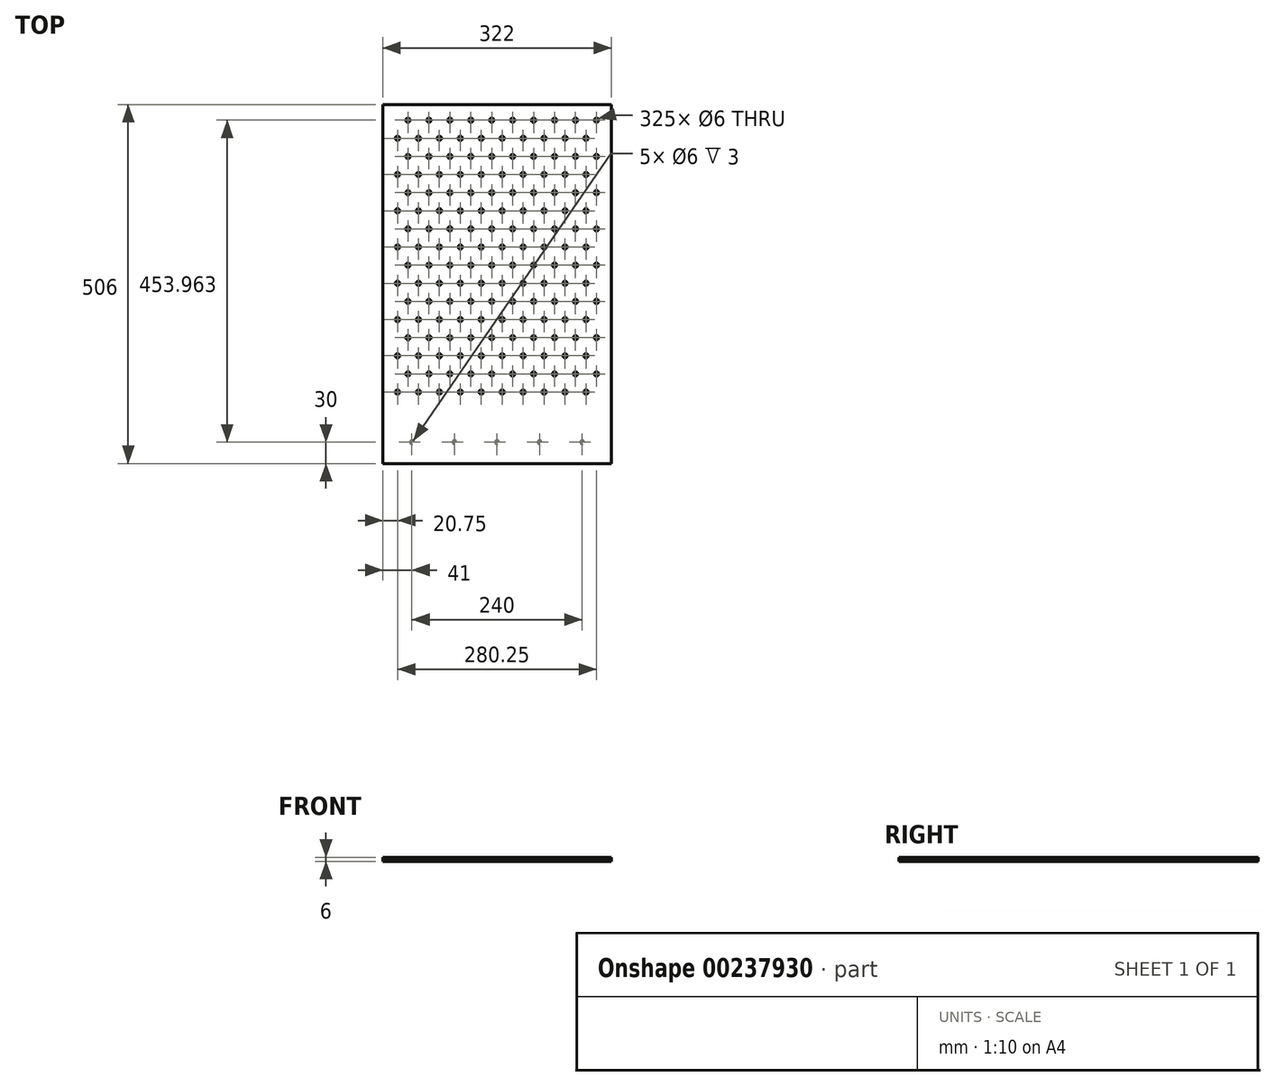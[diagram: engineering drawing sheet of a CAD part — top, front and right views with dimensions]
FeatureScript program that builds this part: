
annotation { "Feature Type Name" : "Feature", "Feature Type Description" : "" }
export const myFeature = defineFeature(function(context is Context, id is Id, definition is map)
    precondition{}
    {
        {
            var Q0;
            Q0=qCreatedBy(makeId("Top.planeOp"),FACE);
            var sketch = newSketch(context, id + "F0", { "sketchPlane" : qUnion([Q0])});
            skCircle(sketch, "E0", {"center": v(0, 0) * mm, "radius": 14.75 * mm, "construction": true});
            skLineSegment(sketch, "E1", {"start": v(-14.75, 59.88) * mm, "end": v(-14.75, -39.27) * mm, "construction": true});
            skLineSegment(sketch, "E2", {"start": v(-42.71, -14.75) * mm, "end": v(49.2, -14.75) * mm, "construction": true});
            skLineSegment(sketch, "E3.direction1", {"start": v(0, 0) * mm, "end": v(29.5, 0) * mm, "construction": true});
            skLineSegment(sketch, "E3.direction2", {"start": v(0, -297.48) * mm, "end": v(0, 0) * mm, "construction": true});
            skCircle(sketch, "E4", {"center": v(0, 0) * mm, "radius": 3 * mm});
            skCircle(sketch, "E5.0.1.0", {"center": v(0, 51.1) * mm, "radius": 3 * mm});
            skCircle(sketch, "E5.0.2.0", {"center": v(0, 102.19) * mm, "radius": 3 * mm});
            skCircle(sketch, "E5.0.3.0", {"center": v(0, 153.28) * mm, "radius": 3 * mm});
            skCircle(sketch, "E5.0.4.0", {"center": v(0, 204.38) * mm, "radius": 3 * mm});
            skCircle(sketch, "E5.0.5.0", {"center": v(0, 255.47) * mm, "radius": 3 * mm});
            skCircle(sketch, "E5.1.0.0", {"center": v(29.5, 0) * mm, "radius": 3 * mm});
            skCircle(sketch, "E5.1.1.0", {"center": v(29.5, 51.1) * mm, "radius": 3 * mm});
            skCircle(sketch, "E5.1.2.0", {"center": v(29.5, 102.19) * mm, "radius": 3 * mm});
            skCircle(sketch, "E5.1.3.0", {"center": v(29.5, 153.28) * mm, "radius": 3 * mm});
            skCircle(sketch, "E5.1.4.0", {"center": v(29.5, 204.38) * mm, "radius": 3 * mm});
            skCircle(sketch, "E5.1.5.0", {"center": v(29.5, 255.47) * mm, "radius": 3 * mm});
            skCircle(sketch, "E5.2.0.0", {"center": v(59, 0) * mm, "radius": 3 * mm});
            skCircle(sketch, "E5.2.1.0", {"center": v(59, 51.1) * mm, "radius": 3 * mm});
            skCircle(sketch, "E5.2.2.0", {"center": v(59, 102.19) * mm, "radius": 3 * mm});
            skCircle(sketch, "E5.2.3.0", {"center": v(59, 153.28) * mm, "radius": 3 * mm});
            skCircle(sketch, "E5.2.4.0", {"center": v(59, 204.38) * mm, "radius": 3 * mm});
            skCircle(sketch, "E5.2.5.0", {"center": v(59, 255.47) * mm, "radius": 3 * mm});
            skCircle(sketch, "E5.3.0.0", {"center": v(88.5, 0) * mm, "radius": 3 * mm});
            skCircle(sketch, "E5.3.1.0", {"center": v(88.5, 51.1) * mm, "radius": 3 * mm});
            skCircle(sketch, "E5.3.2.0", {"center": v(88.5, 102.19) * mm, "radius": 3 * mm});
            skCircle(sketch, "E5.3.3.0", {"center": v(88.5, 153.28) * mm, "radius": 3 * mm});
            skCircle(sketch, "E5.3.4.0", {"center": v(88.5, 204.38) * mm, "radius": 3 * mm});
            skCircle(sketch, "E5.3.5.0", {"center": v(88.5, 255.47) * mm, "radius": 3 * mm});
            skCircle(sketch, "E5.4.0.0", {"center": v(118, 0) * mm, "radius": 3 * mm});
            skCircle(sketch, "E5.4.1.0", {"center": v(118, 51.1) * mm, "radius": 3 * mm});
            skCircle(sketch, "E5.4.2.0", {"center": v(118, 102.19) * mm, "radius": 3 * mm});
            skCircle(sketch, "E5.4.3.0", {"center": v(118, 153.28) * mm, "radius": 3 * mm});
            skCircle(sketch, "E5.4.4.0", {"center": v(118, 204.38) * mm, "radius": 3 * mm});
            skCircle(sketch, "E5.4.5.0", {"center": v(118, 255.47) * mm, "radius": 3 * mm});
            skCircle(sketch, "E5.5.0.0", {"center": v(147.5, 0) * mm, "radius": 3 * mm});
            skCircle(sketch, "E5.5.1.0", {"center": v(147.5, 51.1) * mm, "radius": 3 * mm});
            skCircle(sketch, "E5.5.2.0", {"center": v(147.5, 102.19) * mm, "radius": 3 * mm});
            skCircle(sketch, "E5.5.3.0", {"center": v(147.5, 153.28) * mm, "radius": 3 * mm});
            skCircle(sketch, "E5.5.4.0", {"center": v(147.5, 204.38) * mm, "radius": 3 * mm});
            skCircle(sketch, "E5.5.5.0", {"center": v(147.5, 255.47) * mm, "radius": 3 * mm});
            skCircle(sketch, "E5.6.0.0", {"center": v(177, 0) * mm, "radius": 3 * mm});
            skCircle(sketch, "E5.6.1.0", {"center": v(177, 51.1) * mm, "radius": 3 * mm});
            skCircle(sketch, "E5.6.2.0", {"center": v(177, 102.19) * mm, "radius": 3 * mm});
            skCircle(sketch, "E5.6.3.0", {"center": v(177, 153.28) * mm, "radius": 3 * mm});
            skCircle(sketch, "E5.6.4.0", {"center": v(177, 204.38) * mm, "radius": 3 * mm});
            skCircle(sketch, "E5.6.5.0", {"center": v(177, 255.47) * mm, "radius": 3 * mm});
            skLineSegment(sketch, "E5.direction2", {"start": v(0, 0) * mm, "end": v(0, 51.1) * mm, "construction": true});
            skLineSegment(sketch, "E6", {"start": v(-14.75, -14.75) * mm, "end": v(295.25, -14.75) * mm, "construction": true});
            skPoint(sketch, "E6.endSnap0", {"position": v(3.24, -14.75) * mm});
            skLineSegment(sketch, "E7", {"start": v(295.25, -14.75) * mm, "end": v(295.25, 395.25) * mm, "construction": true});
            skLineSegment(sketch, "E8", {"start": v(295.25, 395.25) * mm, "end": v(-14.75, 395.25) * mm, "construction": true});
            skLineSegment(sketch, "E9", {"start": v(-14.75, 395.25) * mm, "end": v(-14.75, -14.75) * mm, "construction": true});
            skCircle(sketch, "E10.0.7.0", {"center": v(206.5, 0) * mm, "radius": 3 * mm});
            skCircle(sketch, "E10.0.7.1", {"center": v(206.5, 51.1) * mm, "radius": 3 * mm});
            skCircle(sketch, "E10.0.7.2", {"center": v(206.5, 102.19) * mm, "radius": 3 * mm});
            skCircle(sketch, "E10.0.7.3", {"center": v(206.5, 153.28) * mm, "radius": 3 * mm});
            skCircle(sketch, "E10.0.7.4", {"center": v(206.5, 204.38) * mm, "radius": 3 * mm});
            skCircle(sketch, "E10.0.7.5", {"center": v(206.5, 255.47) * mm, "radius": 3 * mm});
            skCircle(sketch, "E10.0.8.0", {"center": v(236, 0) * mm, "radius": 3 * mm});
            skCircle(sketch, "E10.0.8.1", {"center": v(236, 51.1) * mm, "radius": 3 * mm});
            skCircle(sketch, "E10.0.8.2", {"center": v(236, 102.19) * mm, "radius": 3 * mm});
            skCircle(sketch, "E10.0.8.3", {"center": v(236, 153.28) * mm, "radius": 3 * mm});
            skCircle(sketch, "E10.0.8.4", {"center": v(236, 204.38) * mm, "radius": 3 * mm});
            skCircle(sketch, "E10.0.8.5", {"center": v(236, 255.47) * mm, "radius": 3 * mm});
            skCircle(sketch, "E11.0.9.0", {"center": v(265.5, 0) * mm, "radius": 3 * mm});
            skCircle(sketch, "E11.0.9.1", {"center": v(265.5, 51.1) * mm, "radius": 3 * mm});
            skCircle(sketch, "E11.0.9.2", {"center": v(265.5, 102.19) * mm, "radius": 3 * mm});
            skCircle(sketch, "E11.0.9.3", {"center": v(265.5, 153.28) * mm, "radius": 3 * mm});
            skCircle(sketch, "E11.0.9.4", {"center": v(265.5, 204.38) * mm, "radius": 3 * mm});
            skCircle(sketch, "E11.0.9.5", {"center": v(265.5, 255.47) * mm, "radius": 3 * mm});
            skLineSegment(sketch, "E12", {"start": v(-20.75, 405.25) * mm, "end": v(301.25, 405.25) * mm});
            skLineSegment(sketch, "E13", {"start": v(301.25, 405.25) * mm, "end": v(301.25, -100.75) * mm});
            skLineSegment(sketch, "E14", {"start": v(301.25, -100.75) * mm, "end": v(-20.75, -100.75) * mm});
            skLineSegment(sketch, "E15", {"start": v(-20.75, -100.75) * mm, "end": v(-20.75, 405.25) * mm});
            skCircle(sketch, "E16", {"center": v(29.5, 0) * mm, "radius": 14.75 * mm, "construction": true});
            skCircle(sketch, "E17", {"center": v(14.75, 25.55) * mm, "radius": 14.75 * mm, "construction": true});
            skCircle(sketch, "E18", {"center": v(0, 51.1) * mm, "radius": 14.75 * mm, "construction": true});
            skCircle(sketch, "E19.0.0.6", {"center": v(0, 306.57) * mm, "radius": 3 * mm});
            skCircle(sketch, "E19.0.0.7", {"center": v(0, 357.67) * mm, "radius": 3 * mm});
            skCircle(sketch, "E19.0.1.6", {"center": v(29.5, 306.57) * mm, "radius": 3 * mm});
            skCircle(sketch, "E19.0.1.7", {"center": v(29.5, 357.67) * mm, "radius": 3 * mm});
            skCircle(sketch, "E19.0.2.6", {"center": v(59, 306.57) * mm, "radius": 3 * mm});
            skCircle(sketch, "E19.0.2.7", {"center": v(59, 357.67) * mm, "radius": 3 * mm});
            skCircle(sketch, "E19.0.3.6", {"center": v(88.5, 306.57) * mm, "radius": 3 * mm});
            skCircle(sketch, "E19.0.3.7", {"center": v(88.5, 357.67) * mm, "radius": 3 * mm});
            skCircle(sketch, "E19.0.4.6", {"center": v(118, 306.57) * mm, "radius": 3 * mm});
            skCircle(sketch, "E19.0.4.7", {"center": v(118, 357.67) * mm, "radius": 3 * mm});
            skCircle(sketch, "E19.0.5.6", {"center": v(147.5, 306.57) * mm, "radius": 3 * mm});
            skCircle(sketch, "E19.0.5.7", {"center": v(147.5, 357.67) * mm, "radius": 3 * mm});
            skCircle(sketch, "E19.0.6.6", {"center": v(177, 306.57) * mm, "radius": 3 * mm});
            skCircle(sketch, "E19.0.6.7", {"center": v(177, 357.67) * mm, "radius": 3 * mm});
            skCircle(sketch, "E19.0.7.6", {"center": v(206.5, 306.57) * mm, "radius": 3 * mm});
            skCircle(sketch, "E19.0.7.7", {"center": v(206.5, 357.67) * mm, "radius": 3 * mm});
            skCircle(sketch, "E19.0.8.6", {"center": v(236, 306.57) * mm, "radius": 3 * mm});
            skCircle(sketch, "E19.0.8.7", {"center": v(236, 357.67) * mm, "radius": 3 * mm});
            skCircle(sketch, "E19.0.9.6", {"center": v(265.5, 306.57) * mm, "radius": 3 * mm});
            skCircle(sketch, "E19.0.9.7", {"center": v(265.5, 357.67) * mm, "radius": 3 * mm});
            skCircle(sketch, "E20", {"center": v(14.75, 25.55) * mm, "radius": 3 * mm});
            skCircle(sketch, "E21.0.1.0", {"center": v(14.75, 76.64) * mm, "radius": 3 * mm});
            skCircle(sketch, "E21.0.2.0", {"center": v(14.75, 127.74) * mm, "radius": 3 * mm});
            skCircle(sketch, "E21.0.3.0", {"center": v(14.75, 178.83) * mm, "radius": 3 * mm});
            skCircle(sketch, "E21.0.4.0", {"center": v(14.75, 229.93) * mm, "radius": 3 * mm});
            skCircle(sketch, "E21.0.5.0", {"center": v(14.75, 281.02) * mm, "radius": 3 * mm});
            skCircle(sketch, "E21.0.6.0", {"center": v(14.75, 332.12) * mm, "radius": 3 * mm});
            skCircle(sketch, "E21.1.0.0", {"center": v(44.25, 25.55) * mm, "radius": 3 * mm});
            skCircle(sketch, "E21.1.1.0", {"center": v(44.25, 76.64) * mm, "radius": 3 * mm});
            skCircle(sketch, "E21.1.2.0", {"center": v(44.25, 127.74) * mm, "radius": 3 * mm});
            skCircle(sketch, "E21.1.3.0", {"center": v(44.25, 178.83) * mm, "radius": 3 * mm});
            skCircle(sketch, "E21.1.4.0", {"center": v(44.25, 229.93) * mm, "radius": 3 * mm});
            skCircle(sketch, "E21.1.5.0", {"center": v(44.25, 281.02) * mm, "radius": 3 * mm});
            skCircle(sketch, "E21.1.6.0", {"center": v(44.25, 332.12) * mm, "radius": 3 * mm});
            skCircle(sketch, "E21.2.0.0", {"center": v(73.75, 25.55) * mm, "radius": 3 * mm});
            skCircle(sketch, "E21.2.1.0", {"center": v(73.75, 76.64) * mm, "radius": 3 * mm});
            skCircle(sketch, "E21.2.2.0", {"center": v(73.75, 127.74) * mm, "radius": 3 * mm});
            skCircle(sketch, "E21.2.3.0", {"center": v(73.75, 178.83) * mm, "radius": 3 * mm});
            skCircle(sketch, "E21.2.4.0", {"center": v(73.75, 229.93) * mm, "radius": 3 * mm});
            skCircle(sketch, "E21.2.5.0", {"center": v(73.75, 281.02) * mm, "radius": 3 * mm});
            skCircle(sketch, "E21.2.6.0", {"center": v(73.75, 332.12) * mm, "radius": 3 * mm});
            skCircle(sketch, "E21.3.0.0", {"center": v(103.25, 25.55) * mm, "radius": 3 * mm});
            skCircle(sketch, "E21.3.1.0", {"center": v(103.25, 76.64) * mm, "radius": 3 * mm});
            skCircle(sketch, "E21.3.2.0", {"center": v(103.25, 127.74) * mm, "radius": 3 * mm});
            skCircle(sketch, "E21.3.3.0", {"center": v(103.25, 178.83) * mm, "radius": 3 * mm});
            skCircle(sketch, "E21.3.4.0", {"center": v(103.25, 229.93) * mm, "radius": 3 * mm});
            skCircle(sketch, "E21.3.5.0", {"center": v(103.25, 281.02) * mm, "radius": 3 * mm});
            skCircle(sketch, "E21.3.6.0", {"center": v(103.25, 332.12) * mm, "radius": 3 * mm});
            skCircle(sketch, "E21.4.0.0", {"center": v(132.75, 25.55) * mm, "radius": 3 * mm});
            skCircle(sketch, "E21.4.1.0", {"center": v(132.75, 76.64) * mm, "radius": 3 * mm});
            skCircle(sketch, "E21.4.2.0", {"center": v(132.75, 127.74) * mm, "radius": 3 * mm});
            skCircle(sketch, "E21.4.3.0", {"center": v(132.75, 178.83) * mm, "radius": 3 * mm});
            skCircle(sketch, "E21.4.4.0", {"center": v(132.75, 229.93) * mm, "radius": 3 * mm});
            skCircle(sketch, "E21.4.5.0", {"center": v(132.75, 281.02) * mm, "radius": 3 * mm});
            skCircle(sketch, "E21.4.6.0", {"center": v(132.75, 332.12) * mm, "radius": 3 * mm});
            skCircle(sketch, "E21.5.0.0", {"center": v(162.25, 25.55) * mm, "radius": 3 * mm});
            skCircle(sketch, "E21.5.1.0", {"center": v(162.25, 76.64) * mm, "radius": 3 * mm});
            skCircle(sketch, "E21.5.2.0", {"center": v(162.25, 127.74) * mm, "radius": 3 * mm});
            skCircle(sketch, "E21.5.3.0", {"center": v(162.25, 178.83) * mm, "radius": 3 * mm});
            skCircle(sketch, "E21.5.4.0", {"center": v(162.25, 229.93) * mm, "radius": 3 * mm});
            skCircle(sketch, "E21.5.5.0", {"center": v(162.25, 281.02) * mm, "radius": 3 * mm});
            skCircle(sketch, "E21.5.6.0", {"center": v(162.25, 332.12) * mm, "radius": 3 * mm});
            skCircle(sketch, "E21.6.0.0", {"center": v(191.75, 25.55) * mm, "radius": 3 * mm});
            skCircle(sketch, "E21.6.1.0", {"center": v(191.75, 76.64) * mm, "radius": 3 * mm});
            skCircle(sketch, "E21.6.2.0", {"center": v(191.75, 127.74) * mm, "radius": 3 * mm});
            skCircle(sketch, "E21.6.3.0", {"center": v(191.75, 178.83) * mm, "radius": 3 * mm});
            skCircle(sketch, "E21.6.4.0", {"center": v(191.75, 229.93) * mm, "radius": 3 * mm});
            skCircle(sketch, "E21.6.5.0", {"center": v(191.75, 281.02) * mm, "radius": 3 * mm});
            skCircle(sketch, "E21.6.6.0", {"center": v(191.75, 332.12) * mm, "radius": 3 * mm});
            skCircle(sketch, "E21.7.0.0", {"center": v(221.25, 25.55) * mm, "radius": 3 * mm});
            skCircle(sketch, "E21.7.1.0", {"center": v(221.25, 76.64) * mm, "radius": 3 * mm});
            skCircle(sketch, "E21.7.2.0", {"center": v(221.25, 127.74) * mm, "radius": 3 * mm});
            skCircle(sketch, "E21.7.3.0", {"center": v(221.25, 178.83) * mm, "radius": 3 * mm});
            skCircle(sketch, "E21.7.4.0", {"center": v(221.25, 229.93) * mm, "radius": 3 * mm});
            skCircle(sketch, "E21.7.5.0", {"center": v(221.25, 281.02) * mm, "radius": 3 * mm});
            skCircle(sketch, "E21.7.6.0", {"center": v(221.25, 332.12) * mm, "radius": 3 * mm});
            skCircle(sketch, "E21.8.0.0", {"center": v(250.75, 25.55) * mm, "radius": 3 * mm});
            skCircle(sketch, "E21.8.1.0", {"center": v(250.75, 76.64) * mm, "radius": 3 * mm});
            skCircle(sketch, "E21.8.2.0", {"center": v(250.75, 127.74) * mm, "radius": 3 * mm});
            skCircle(sketch, "E21.8.3.0", {"center": v(250.75, 178.83) * mm, "radius": 3 * mm});
            skCircle(sketch, "E21.8.4.0", {"center": v(250.75, 229.93) * mm, "radius": 3 * mm});
            skCircle(sketch, "E21.8.5.0", {"center": v(250.75, 281.02) * mm, "radius": 3 * mm});
            skCircle(sketch, "E21.8.6.0", {"center": v(250.75, 332.12) * mm, "radius": 3 * mm});
            skCircle(sketch, "E21.9.0.0", {"center": v(280.25, 25.55) * mm, "radius": 3 * mm});
            skCircle(sketch, "E21.9.1.0", {"center": v(280.25, 76.64) * mm, "radius": 3 * mm});
            skCircle(sketch, "E21.9.2.0", {"center": v(280.25, 127.74) * mm, "radius": 3 * mm});
            skCircle(sketch, "E21.9.3.0", {"center": v(280.25, 178.83) * mm, "radius": 3 * mm});
            skCircle(sketch, "E21.9.4.0", {"center": v(280.25, 229.93) * mm, "radius": 3 * mm});
            skCircle(sketch, "E21.9.5.0", {"center": v(280.25, 281.02) * mm, "radius": 3 * mm});
            skCircle(sketch, "E21.9.6.0", {"center": v(280.25, 332.12) * mm, "radius": 3 * mm});
            skLineSegment(sketch, "E21.direction1", {"start": v(14.75, 25.55) * mm, "end": v(44.25, 25.55) * mm, "construction": true});
            skLineSegment(sketch, "E21.direction2", {"start": v(14.75, 25.55) * mm, "end": v(14.75, 76.64) * mm, "construction": true});
            skCircle(sketch, "E22", {"center": v(59, 119.22) * mm, "radius": 14.03 * mm, "construction": true});
            skLineSegment(sketch, "E23.bottom", {"start": v(54, 129.22) * mm, "end": v(64, 129.22) * mm, "construction": true});
            skLineSegment(sketch, "E23.top", {"start": v(54, 109.22) * mm, "end": v(64, 109.22) * mm, "construction": true});
            skLineSegment(sketch, "E23.left", {"start": v(54, 129.22) * mm, "end": v(54, 109.22) * mm, "construction": true});
            skLineSegment(sketch, "E23.right", {"start": v(64, 129.22) * mm, "end": v(64, 109.22) * mm, "construction": true});
            skPoint(sketch, "E24.positionSnap0", {"position": v(54, 119.22) * mm});
            skPoint(sketch, "E24.positionSnap1", {"position": v(59, 129.22) * mm});
            skCircle(sketch, "E25.0.0.7", {"center": v(14.75, 383.21) * mm, "radius": 3 * mm});
            skCircle(sketch, "E25.0.1.7", {"center": v(44.25, 383.21) * mm, "radius": 3 * mm});
            skCircle(sketch, "E25.0.2.7", {"center": v(73.75, 383.21) * mm, "radius": 3 * mm});
            skCircle(sketch, "E25.0.3.7", {"center": v(103.25, 383.21) * mm, "radius": 3 * mm});
            skCircle(sketch, "E25.0.4.7", {"center": v(132.75, 383.21) * mm, "radius": 3 * mm});
            skCircle(sketch, "E25.0.5.7", {"center": v(162.25, 383.21) * mm, "radius": 3 * mm});
            skCircle(sketch, "E25.0.6.7", {"center": v(191.75, 383.21) * mm, "radius": 3 * mm});
            skCircle(sketch, "E25.0.7.7", {"center": v(221.25, 383.21) * mm, "radius": 3 * mm});
            skCircle(sketch, "E25.0.8.7", {"center": v(250.75, 383.21) * mm, "radius": 3 * mm});
            skCircle(sketch, "E25.0.9.7", {"center": v(280.25, 383.21) * mm, "radius": 3 * mm});
            skCircle(sketch, "E26", {"center": v(14.75, 383.21) * mm, "radius": 14.75 * mm, "construction": true});
            skCircle(sketch, "E27", {"center": v(280.25, 25.55) * mm, "radius": 14.75 * mm, "construction": true});
            skSolve(sketch);
        }
        {
            var Q0;
            Q0=makeQuery(id+"F0.imprint","IMPRINT",FACE,{"disambiguationData":[TD([[makeQuery(id+"F0.imprint","IMPRINT",EDGE,{"derivedFrom":sQuery(id+"F0.wireOp",EDGE,"E4")}),-1.0]])]});
            extrude(context, id + "F1", {"entities" : qUnion([Q0]), "depth" : 5 * mm});
        }
        {
            var Q0;
            Q0=makeQuery(id+"F1.opExtrude","CAP_FACE",FACE,{"disambiguationData":[OSD([sQuery(id+"F0.wireOp",EDGE,"E4"),sQuery(id+"F0.wireOp",EDGE,"E5.0.1.0"),sQuery(id+"F0.wireOp",EDGE,"E5.0.2.0"),sQuery(id+"F0.wireOp",EDGE,"E5.0.3.0"),sQuery(id+"F0.wireOp",EDGE,"E5.0.4.0"),sQuery(id+"F0.wireOp",EDGE,"E5.0.5.0"),sQuery(id+"F0.wireOp",EDGE,"E5.1.0.0"),sQuery(id+"F0.wireOp",EDGE,"E5.1.1.0"),sQuery(id+"F0.wireOp",EDGE,"E5.1.2.0"),sQuery(id+"F0.wireOp",EDGE,"E5.1.3.0"),sQuery(id+"F0.wireOp",EDGE,"E5.1.4.0"),sQuery(id+"F0.wireOp",EDGE,"E5.1.5.0"),sQuery(id+"F0.wireOp",EDGE,"E5.2.0.0"),sQuery(id+"F0.wireOp",EDGE,"E5.2.1.0"),sQuery(id+"F0.wireOp",EDGE,"E5.2.2.0"),sQuery(id+"F0.wireOp",EDGE,"E5.2.3.0"),sQuery(id+"F0.wireOp",EDGE,"E5.2.4.0"),sQuery(id+"F0.wireOp",EDGE,"E5.2.5.0"),sQuery(id+"F0.wireOp",EDGE,"E5.3.0.0"),sQuery(id+"F0.wireOp",EDGE,"E5.3.1.0"),sQuery(id+"F0.wireOp",EDGE,"E5.3.2.0"),sQuery(id+"F0.wireOp",EDGE,"E5.3.3.0"),sQuery(id+"F0.wireOp",EDGE,"E5.3.4.0"),sQuery(id+"F0.wireOp",EDGE,"E5.3.5.0"),sQuery(id+"F0.wireOp",EDGE,"E5.4.0.0"),sQuery(id+"F0.wireOp",EDGE,"E5.4.1.0"),sQuery(id+"F0.wireOp",EDGE,"E5.4.2.0"),sQuery(id+"F0.wireOp",EDGE,"E5.4.3.0"),sQuery(id+"F0.wireOp",EDGE,"E5.4.4.0"),sQuery(id+"F0.wireOp",EDGE,"E5.4.5.0"),sQuery(id+"F0.wireOp",EDGE,"E5.5.0.0"),sQuery(id+"F0.wireOp",EDGE,"E5.5.1.0"),sQuery(id+"F0.wireOp",EDGE,"E5.5.2.0"),sQuery(id+"F0.wireOp",EDGE,"E5.5.3.0"),sQuery(id+"F0.wireOp",EDGE,"E5.5.4.0"),sQuery(id+"F0.wireOp",EDGE,"E5.5.5.0"),sQuery(id+"F0.wireOp",EDGE,"E5.6.0.0"),sQuery(id+"F0.wireOp",EDGE,"E5.6.1.0"),sQuery(id+"F0.wireOp",EDGE,"E5.6.2.0"),sQuery(id+"F0.wireOp",EDGE,"E5.6.3.0"),sQuery(id+"F0.wireOp",EDGE,"E5.6.4.0"),sQuery(id+"F0.wireOp",EDGE,"E5.6.5.0"),sQuery(id+"F0.wireOp",EDGE,"E10.0.7.0"),sQuery(id+"F0.wireOp",EDGE,"E10.0.7.1"),sQuery(id+"F0.wireOp",EDGE,"E10.0.7.2"),sQuery(id+"F0.wireOp",EDGE,"E10.0.7.3"),sQuery(id+"F0.wireOp",EDGE,"E10.0.7.4"),sQuery(id+"F0.wireOp",EDGE,"E10.0.7.5"),sQuery(id+"F0.wireOp",EDGE,"E10.0.8.0"),sQuery(id+"F0.wireOp",EDGE,"E10.0.8.1"),sQuery(id+"F0.wireOp",EDGE,"E10.0.8.2"),sQuery(id+"F0.wireOp",EDGE,"E10.0.8.3"),sQuery(id+"F0.wireOp",EDGE,"E10.0.8.4"),sQuery(id+"F0.wireOp",EDGE,"E10.0.8.5"),sQuery(id+"F0.wireOp",EDGE,"E11.0.9.0"),sQuery(id+"F0.wireOp",EDGE,"E11.0.9.1"),sQuery(id+"F0.wireOp",EDGE,"E11.0.9.2"),sQuery(id+"F0.wireOp",EDGE,"E11.0.9.3"),sQuery(id+"F0.wireOp",EDGE,"E11.0.9.4"),sQuery(id+"F0.wireOp",EDGE,"E11.0.9.5"),sQuery(id+"F0.wireOp",EDGE,"E12"),sQuery(id+"F0.wireOp",EDGE,"E13"),sQuery(id+"F0.wireOp",EDGE,"E14"),sQuery(id+"F0.wireOp",EDGE,"E15"),sQuery(id+"F0.wireOp",EDGE,"E19.0.0.6"),sQuery(id+"F0.wireOp",EDGE,"E19.0.0.7"),sQuery(id+"F0.wireOp",EDGE,"E19.0.1.6"),sQuery(id+"F0.wireOp",EDGE,"E19.0.1.7"),sQuery(id+"F0.wireOp",EDGE,"E19.0.2.6"),sQuery(id+"F0.wireOp",EDGE,"E19.0.2.7"),sQuery(id+"F0.wireOp",EDGE,"E19.0.3.6"),sQuery(id+"F0.wireOp",EDGE,"E19.0.3.7"),sQuery(id+"F0.wireOp",EDGE,"E19.0.4.6"),sQuery(id+"F0.wireOp",EDGE,"E19.0.4.7"),sQuery(id+"F0.wireOp",EDGE,"E19.0.5.6"),sQuery(id+"F0.wireOp",EDGE,"E19.0.5.7"),sQuery(id+"F0.wireOp",EDGE,"E19.0.6.6"),sQuery(id+"F0.wireOp",EDGE,"E19.0.6.7"),sQuery(id+"F0.wireOp",EDGE,"E19.0.7.6"),sQuery(id+"F0.wireOp",EDGE,"E19.0.7.7"),sQuery(id+"F0.wireOp",EDGE,"E19.0.8.6"),sQuery(id+"F0.wireOp",EDGE,"E19.0.8.7"),sQuery(id+"F0.wireOp",EDGE,"E19.0.9.6"),sQuery(id+"F0.wireOp",EDGE,"E19.0.9.7"),sQuery(id+"F0.wireOp",EDGE,"E20"),sQuery(id+"F0.wireOp",EDGE,"E21.0.1.0"),sQuery(id+"F0.wireOp",EDGE,"E21.0.2.0"),sQuery(id+"F0.wireOp",EDGE,"E21.0.3.0"),sQuery(id+"F0.wireOp",EDGE,"E21.0.4.0"),sQuery(id+"F0.wireOp",EDGE,"E21.0.5.0"),sQuery(id+"F0.wireOp",EDGE,"E21.0.6.0"),sQuery(id+"F0.wireOp",EDGE,"E21.1.0.0"),sQuery(id+"F0.wireOp",EDGE,"E21.1.1.0"),sQuery(id+"F0.wireOp",EDGE,"E21.1.2.0"),sQuery(id+"F0.wireOp",EDGE,"E21.1.3.0"),sQuery(id+"F0.wireOp",EDGE,"E21.1.4.0"),sQuery(id+"F0.wireOp",EDGE,"E21.1.5.0"),sQuery(id+"F0.wireOp",EDGE,"E21.1.6.0"),sQuery(id+"F0.wireOp",EDGE,"E21.2.0.0"),sQuery(id+"F0.wireOp",EDGE,"E21.2.1.0"),sQuery(id+"F0.wireOp",EDGE,"E21.2.2.0"),sQuery(id+"F0.wireOp",EDGE,"E21.2.3.0"),sQuery(id+"F0.wireOp",EDGE,"E21.2.4.0"),sQuery(id+"F0.wireOp",EDGE,"E21.2.5.0"),sQuery(id+"F0.wireOp",EDGE,"E21.2.6.0"),sQuery(id+"F0.wireOp",EDGE,"E21.3.0.0"),sQuery(id+"F0.wireOp",EDGE,"E21.3.1.0"),sQuery(id+"F0.wireOp",EDGE,"E21.3.2.0"),sQuery(id+"F0.wireOp",EDGE,"E21.3.3.0"),sQuery(id+"F0.wireOp",EDGE,"E21.3.4.0"),sQuery(id+"F0.wireOp",EDGE,"E21.3.5.0"),sQuery(id+"F0.wireOp",EDGE,"E21.3.6.0"),sQuery(id+"F0.wireOp",EDGE,"E21.4.0.0"),sQuery(id+"F0.wireOp",EDGE,"E21.4.1.0"),sQuery(id+"F0.wireOp",EDGE,"E21.4.2.0"),sQuery(id+"F0.wireOp",EDGE,"E21.4.3.0"),sQuery(id+"F0.wireOp",EDGE,"E21.4.4.0"),sQuery(id+"F0.wireOp",EDGE,"E21.4.5.0"),sQuery(id+"F0.wireOp",EDGE,"E21.4.6.0"),sQuery(id+"F0.wireOp",EDGE,"E21.5.0.0"),sQuery(id+"F0.wireOp",EDGE,"E21.5.1.0"),sQuery(id+"F0.wireOp",EDGE,"E21.5.2.0"),sQuery(id+"F0.wireOp",EDGE,"E21.5.3.0"),sQuery(id+"F0.wireOp",EDGE,"E21.5.4.0"),sQuery(id+"F0.wireOp",EDGE,"E21.5.5.0"),sQuery(id+"F0.wireOp",EDGE,"E21.5.6.0"),sQuery(id+"F0.wireOp",EDGE,"E21.6.0.0"),sQuery(id+"F0.wireOp",EDGE,"E21.6.1.0"),sQuery(id+"F0.wireOp",EDGE,"E21.6.2.0"),sQuery(id+"F0.wireOp",EDGE,"E21.6.3.0"),sQuery(id+"F0.wireOp",EDGE,"E21.6.4.0"),sQuery(id+"F0.wireOp",EDGE,"E21.6.5.0"),sQuery(id+"F0.wireOp",EDGE,"E21.6.6.0"),sQuery(id+"F0.wireOp",EDGE,"E21.7.0.0"),sQuery(id+"F0.wireOp",EDGE,"E21.7.1.0"),sQuery(id+"F0.wireOp",EDGE,"E21.7.2.0"),sQuery(id+"F0.wireOp",EDGE,"E21.7.3.0"),sQuery(id+"F0.wireOp",EDGE,"E21.7.4.0"),sQuery(id+"F0.wireOp",EDGE,"E21.7.5.0"),sQuery(id+"F0.wireOp",EDGE,"E21.7.6.0"),sQuery(id+"F0.wireOp",EDGE,"E21.8.0.0"),sQuery(id+"F0.wireOp",EDGE,"E21.8.1.0"),sQuery(id+"F0.wireOp",EDGE,"E21.8.2.0"),sQuery(id+"F0.wireOp",EDGE,"E21.8.3.0"),sQuery(id+"F0.wireOp",EDGE,"E21.8.4.0"),sQuery(id+"F0.wireOp",EDGE,"E21.8.5.0"),sQuery(id+"F0.wireOp",EDGE,"E21.8.6.0"),sQuery(id+"F0.wireOp",EDGE,"E21.9.0.0"),sQuery(id+"F0.wireOp",EDGE,"E21.9.1.0"),sQuery(id+"F0.wireOp",EDGE,"E21.9.2.0"),sQuery(id+"F0.wireOp",EDGE,"E21.9.3.0"),sQuery(id+"F0.wireOp",EDGE,"E21.9.4.0"),sQuery(id+"F0.wireOp",EDGE,"E21.9.5.0"),sQuery(id+"F0.wireOp",EDGE,"E21.9.6.0"),sQuery(id+"F0.wireOp",EDGE,"E25.0.0.7"),sQuery(id+"F0.wireOp",EDGE,"E25.0.1.7"),sQuery(id+"F0.wireOp",EDGE,"E25.0.2.7"),sQuery(id+"F0.wireOp",EDGE,"E25.0.3.7"),sQuery(id+"F0.wireOp",EDGE,"E25.0.4.7"),sQuery(id+"F0.wireOp",EDGE,"E25.0.5.7"),sQuery(id+"F0.wireOp",EDGE,"E25.0.6.7"),sQuery(id+"F0.wireOp",EDGE,"E25.0.7.7"),sQuery(id+"F0.wireOp",EDGE,"E25.0.8.7"),sQuery(id+"F0.wireOp",EDGE,"E25.0.9.7")])],"isStart":true});
            var sketch = newSketch(context, id + "F2", { "sketchPlane" : qUnion([Q0])});
            skCircle(sketch, "E28", {"center": v(20.25, 70.75) * mm, "radius": 3 * mm});
            skCircle(sketch, "E29.1.0.0", {"center": v(80.25, 70.75) * mm, "radius": 3 * mm});
            skCircle(sketch, "E29.2.0.0", {"center": v(140.25, 70.75) * mm, "radius": 3 * mm});
            skCircle(sketch, "E29.3.0.0", {"center": v(200.25, 70.75) * mm, "radius": 3 * mm});
            skCircle(sketch, "E29.4.0.0", {"center": v(260.25, 70.75) * mm, "radius": 3 * mm});
            skLineSegment(sketch, "E29.direction1", {"start": v(20.25, 70.75) * mm, "end": v(80.25, 70.75) * mm, "construction": true});
            skLineSegment(sketch, "E30", {"start": v(20.25, 70.75) * mm, "end": v(-20.75, 70.75) * mm, "construction": true});
            skLineSegment(sketch, "E31", {"start": v(260.25, 70.75) * mm, "end": v(301.25, 70.75) * mm, "construction": true});
            skSolve(sketch);
        }
        {
            var Q0;
            Q0=makeQuery(id+"F2.imprint","IMPRINT",FACE,{"disambiguationData":[TD([[makeQuery(id+"F2.imprint","IMPRINT",EDGE,{"derivedFrom":sQuery(id+"F2.wireOp",EDGE,"E28")}),1.0]])]});
            var Q1;
            Q1=makeQuery(id+"F2.imprint","IMPRINT",FACE,{"disambiguationData":[TD([[makeQuery(id+"F2.imprint","IMPRINT",EDGE,{"derivedFrom":sQuery(id+"F2.wireOp",EDGE,"E29.1.0.0")}),1.0]])]});
            var Q2;
            Q2=makeQuery(id+"F2.imprint","IMPRINT",FACE,{"disambiguationData":[TD([[makeQuery(id+"F2.imprint","IMPRINT",EDGE,{"derivedFrom":sQuery(id+"F2.wireOp",EDGE,"E29.2.0.0")}),1.0]])]});
            var Q3;
            Q3=makeQuery(id+"F2.imprint","IMPRINT",FACE,{"disambiguationData":[TD([[makeQuery(id+"F2.imprint","IMPRINT",EDGE,{"derivedFrom":sQuery(id+"F2.wireOp",EDGE,"E29.3.0.0")}),1.0]])]});
            var Q4;
            Q4=makeQuery(id+"F2.imprint","IMPRINT",FACE,{"disambiguationData":[TD([[makeQuery(id+"F2.imprint","IMPRINT",EDGE,{"derivedFrom":sQuery(id+"F2.wireOp",EDGE,"E29.4.0.0")}),1.0]])]});
            extrude(context, id + "F3", {"entities" : qUnion([Q0, Q1, Q2, Q3, Q4]), "operationType" : NewBodyOperationType.REMOVE, "oppositeDirection" : true, "offsetDistance" : 25 * mm, "depth" : 3 * mm});
        }
        {
            var Q0;
            Q0=makeQuery(id+"F1.opExtrude","CAP_FACE",FACE,{"disambiguationData":[OSD([sQuery(id+"F0.wireOp",EDGE,"E4"),sQuery(id+"F0.wireOp",EDGE,"E5.0.1.0"),sQuery(id+"F0.wireOp",EDGE,"E5.0.2.0"),sQuery(id+"F0.wireOp",EDGE,"E5.0.3.0"),sQuery(id+"F0.wireOp",EDGE,"E5.0.4.0"),sQuery(id+"F0.wireOp",EDGE,"E5.0.5.0"),sQuery(id+"F0.wireOp",EDGE,"E5.1.0.0"),sQuery(id+"F0.wireOp",EDGE,"E5.1.1.0"),sQuery(id+"F0.wireOp",EDGE,"E5.1.2.0"),sQuery(id+"F0.wireOp",EDGE,"E5.1.3.0"),sQuery(id+"F0.wireOp",EDGE,"E5.1.4.0"),sQuery(id+"F0.wireOp",EDGE,"E5.1.5.0"),sQuery(id+"F0.wireOp",EDGE,"E5.2.0.0"),sQuery(id+"F0.wireOp",EDGE,"E5.2.1.0"),sQuery(id+"F0.wireOp",EDGE,"E5.2.2.0"),sQuery(id+"F0.wireOp",EDGE,"E5.2.3.0"),sQuery(id+"F0.wireOp",EDGE,"E5.2.4.0"),sQuery(id+"F0.wireOp",EDGE,"E5.2.5.0"),sQuery(id+"F0.wireOp",EDGE,"E5.3.0.0"),sQuery(id+"F0.wireOp",EDGE,"E5.3.1.0"),sQuery(id+"F0.wireOp",EDGE,"E5.3.2.0"),sQuery(id+"F0.wireOp",EDGE,"E5.3.3.0"),sQuery(id+"F0.wireOp",EDGE,"E5.3.4.0"),sQuery(id+"F0.wireOp",EDGE,"E5.3.5.0"),sQuery(id+"F0.wireOp",EDGE,"E5.4.0.0"),sQuery(id+"F0.wireOp",EDGE,"E5.4.1.0"),sQuery(id+"F0.wireOp",EDGE,"E5.4.2.0"),sQuery(id+"F0.wireOp",EDGE,"E5.4.3.0"),sQuery(id+"F0.wireOp",EDGE,"E5.4.4.0"),sQuery(id+"F0.wireOp",EDGE,"E5.4.5.0"),sQuery(id+"F0.wireOp",EDGE,"E5.5.0.0"),sQuery(id+"F0.wireOp",EDGE,"E5.5.1.0"),sQuery(id+"F0.wireOp",EDGE,"E5.5.2.0"),sQuery(id+"F0.wireOp",EDGE,"E5.5.3.0"),sQuery(id+"F0.wireOp",EDGE,"E5.5.4.0"),sQuery(id+"F0.wireOp",EDGE,"E5.5.5.0"),sQuery(id+"F0.wireOp",EDGE,"E5.6.0.0"),sQuery(id+"F0.wireOp",EDGE,"E5.6.1.0"),sQuery(id+"F0.wireOp",EDGE,"E5.6.2.0"),sQuery(id+"F0.wireOp",EDGE,"E5.6.3.0"),sQuery(id+"F0.wireOp",EDGE,"E5.6.4.0"),sQuery(id+"F0.wireOp",EDGE,"E5.6.5.0"),sQuery(id+"F0.wireOp",EDGE,"E10.0.7.0"),sQuery(id+"F0.wireOp",EDGE,"E10.0.7.1"),sQuery(id+"F0.wireOp",EDGE,"E10.0.7.2"),sQuery(id+"F0.wireOp",EDGE,"E10.0.7.3"),sQuery(id+"F0.wireOp",EDGE,"E10.0.7.4"),sQuery(id+"F0.wireOp",EDGE,"E10.0.7.5"),sQuery(id+"F0.wireOp",EDGE,"E10.0.8.0"),sQuery(id+"F0.wireOp",EDGE,"E10.0.8.1"),sQuery(id+"F0.wireOp",EDGE,"E10.0.8.2"),sQuery(id+"F0.wireOp",EDGE,"E10.0.8.3"),sQuery(id+"F0.wireOp",EDGE,"E10.0.8.4"),sQuery(id+"F0.wireOp",EDGE,"E10.0.8.5"),sQuery(id+"F0.wireOp",EDGE,"E11.0.9.0"),sQuery(id+"F0.wireOp",EDGE,"E11.0.9.1"),sQuery(id+"F0.wireOp",EDGE,"E11.0.9.2"),sQuery(id+"F0.wireOp",EDGE,"E11.0.9.3"),sQuery(id+"F0.wireOp",EDGE,"E11.0.9.4"),sQuery(id+"F0.wireOp",EDGE,"E11.0.9.5"),sQuery(id+"F0.wireOp",EDGE,"E12"),sQuery(id+"F0.wireOp",EDGE,"E13"),sQuery(id+"F0.wireOp",EDGE,"E14"),sQuery(id+"F0.wireOp",EDGE,"E15"),sQuery(id+"F0.wireOp",EDGE,"E19.0.0.6"),sQuery(id+"F0.wireOp",EDGE,"E19.0.0.7"),sQuery(id+"F0.wireOp",EDGE,"E19.0.1.6"),sQuery(id+"F0.wireOp",EDGE,"E19.0.1.7"),sQuery(id+"F0.wireOp",EDGE,"E19.0.2.6"),sQuery(id+"F0.wireOp",EDGE,"E19.0.2.7"),sQuery(id+"F0.wireOp",EDGE,"E19.0.3.6"),sQuery(id+"F0.wireOp",EDGE,"E19.0.3.7"),sQuery(id+"F0.wireOp",EDGE,"E19.0.4.6"),sQuery(id+"F0.wireOp",EDGE,"E19.0.4.7"),sQuery(id+"F0.wireOp",EDGE,"E19.0.5.6"),sQuery(id+"F0.wireOp",EDGE,"E19.0.5.7"),sQuery(id+"F0.wireOp",EDGE,"E19.0.6.6"),sQuery(id+"F0.wireOp",EDGE,"E19.0.6.7"),sQuery(id+"F0.wireOp",EDGE,"E19.0.7.6"),sQuery(id+"F0.wireOp",EDGE,"E19.0.7.7"),sQuery(id+"F0.wireOp",EDGE,"E19.0.8.6"),sQuery(id+"F0.wireOp",EDGE,"E19.0.8.7"),sQuery(id+"F0.wireOp",EDGE,"E19.0.9.6"),sQuery(id+"F0.wireOp",EDGE,"E19.0.9.7"),sQuery(id+"F0.wireOp",EDGE,"E20"),sQuery(id+"F0.wireOp",EDGE,"E21.0.1.0"),sQuery(id+"F0.wireOp",EDGE,"E21.0.2.0"),sQuery(id+"F0.wireOp",EDGE,"E21.0.3.0"),sQuery(id+"F0.wireOp",EDGE,"E21.0.4.0"),sQuery(id+"F0.wireOp",EDGE,"E21.0.5.0"),sQuery(id+"F0.wireOp",EDGE,"E21.0.6.0"),sQuery(id+"F0.wireOp",EDGE,"E21.1.0.0"),sQuery(id+"F0.wireOp",EDGE,"E21.1.1.0"),sQuery(id+"F0.wireOp",EDGE,"E21.1.2.0"),sQuery(id+"F0.wireOp",EDGE,"E21.1.3.0"),sQuery(id+"F0.wireOp",EDGE,"E21.1.4.0"),sQuery(id+"F0.wireOp",EDGE,"E21.1.5.0"),sQuery(id+"F0.wireOp",EDGE,"E21.1.6.0"),sQuery(id+"F0.wireOp",EDGE,"E21.2.0.0"),sQuery(id+"F0.wireOp",EDGE,"E21.2.1.0"),sQuery(id+"F0.wireOp",EDGE,"E21.2.2.0"),sQuery(id+"F0.wireOp",EDGE,"E21.2.3.0"),sQuery(id+"F0.wireOp",EDGE,"E21.2.4.0"),sQuery(id+"F0.wireOp",EDGE,"E21.2.5.0"),sQuery(id+"F0.wireOp",EDGE,"E21.2.6.0"),sQuery(id+"F0.wireOp",EDGE,"E21.3.0.0"),sQuery(id+"F0.wireOp",EDGE,"E21.3.1.0"),sQuery(id+"F0.wireOp",EDGE,"E21.3.2.0"),sQuery(id+"F0.wireOp",EDGE,"E21.3.3.0"),sQuery(id+"F0.wireOp",EDGE,"E21.3.4.0"),sQuery(id+"F0.wireOp",EDGE,"E21.3.5.0"),sQuery(id+"F0.wireOp",EDGE,"E21.3.6.0"),sQuery(id+"F0.wireOp",EDGE,"E21.4.0.0"),sQuery(id+"F0.wireOp",EDGE,"E21.4.1.0"),sQuery(id+"F0.wireOp",EDGE,"E21.4.2.0"),sQuery(id+"F0.wireOp",EDGE,"E21.4.3.0"),sQuery(id+"F0.wireOp",EDGE,"E21.4.4.0"),sQuery(id+"F0.wireOp",EDGE,"E21.4.5.0"),sQuery(id+"F0.wireOp",EDGE,"E21.4.6.0"),sQuery(id+"F0.wireOp",EDGE,"E21.5.0.0"),sQuery(id+"F0.wireOp",EDGE,"E21.5.1.0"),sQuery(id+"F0.wireOp",EDGE,"E21.5.2.0"),sQuery(id+"F0.wireOp",EDGE,"E21.5.3.0"),sQuery(id+"F0.wireOp",EDGE,"E21.5.4.0"),sQuery(id+"F0.wireOp",EDGE,"E21.5.5.0"),sQuery(id+"F0.wireOp",EDGE,"E21.5.6.0"),sQuery(id+"F0.wireOp",EDGE,"E21.6.0.0"),sQuery(id+"F0.wireOp",EDGE,"E21.6.1.0"),sQuery(id+"F0.wireOp",EDGE,"E21.6.2.0"),sQuery(id+"F0.wireOp",EDGE,"E21.6.3.0"),sQuery(id+"F0.wireOp",EDGE,"E21.6.4.0"),sQuery(id+"F0.wireOp",EDGE,"E21.6.5.0"),sQuery(id+"F0.wireOp",EDGE,"E21.6.6.0"),sQuery(id+"F0.wireOp",EDGE,"E21.7.0.0"),sQuery(id+"F0.wireOp",EDGE,"E21.7.1.0"),sQuery(id+"F0.wireOp",EDGE,"E21.7.2.0"),sQuery(id+"F0.wireOp",EDGE,"E21.7.3.0"),sQuery(id+"F0.wireOp",EDGE,"E21.7.4.0"),sQuery(id+"F0.wireOp",EDGE,"E21.7.5.0"),sQuery(id+"F0.wireOp",EDGE,"E21.7.6.0"),sQuery(id+"F0.wireOp",EDGE,"E21.8.0.0"),sQuery(id+"F0.wireOp",EDGE,"E21.8.1.0"),sQuery(id+"F0.wireOp",EDGE,"E21.8.2.0"),sQuery(id+"F0.wireOp",EDGE,"E21.8.3.0"),sQuery(id+"F0.wireOp",EDGE,"E21.8.4.0"),sQuery(id+"F0.wireOp",EDGE,"E21.8.5.0"),sQuery(id+"F0.wireOp",EDGE,"E21.8.6.0"),sQuery(id+"F0.wireOp",EDGE,"E21.9.0.0"),sQuery(id+"F0.wireOp",EDGE,"E21.9.1.0"),sQuery(id+"F0.wireOp",EDGE,"E21.9.2.0"),sQuery(id+"F0.wireOp",EDGE,"E21.9.3.0"),sQuery(id+"F0.wireOp",EDGE,"E21.9.4.0"),sQuery(id+"F0.wireOp",EDGE,"E21.9.5.0"),sQuery(id+"F0.wireOp",EDGE,"E21.9.6.0"),sQuery(id+"F0.wireOp",EDGE,"E25.0.0.7"),sQuery(id+"F0.wireOp",EDGE,"E25.0.1.7"),sQuery(id+"F0.wireOp",EDGE,"E25.0.2.7"),sQuery(id+"F0.wireOp",EDGE,"E25.0.3.7"),sQuery(id+"F0.wireOp",EDGE,"E25.0.4.7"),sQuery(id+"F0.wireOp",EDGE,"E25.0.5.7"),sQuery(id+"F0.wireOp",EDGE,"E25.0.6.7"),sQuery(id+"F0.wireOp",EDGE,"E25.0.7.7"),sQuery(id+"F0.wireOp",EDGE,"E25.0.8.7"),sQuery(id+"F0.wireOp",EDGE,"E25.0.9.7")])],"isStart":true});
            var sketch = newSketch(context, id + "F4", { "sketchPlane" : qUnion([Q0])});
            skLineSegment(sketch, "E32.0", {"start": v(301.25, -405.25) * mm, "end": v(301.25, 100.75) * mm});
            skLineSegment(sketch, "E32.1", {"start": v(-20.75, -405.25) * mm, "end": v(301.25, -405.25) * mm});
            skLineSegment(sketch, "E32.2", {"start": v(-20.75, 100.75) * mm, "end": v(-20.75, -405.25) * mm});
            skLineSegment(sketch, "E32.3", {"start": v(301.25, 100.75) * mm, "end": v(-20.75, 100.75) * mm});
            skSolve(sketch);
        }
        {
            var Q0;
            Q0=makeQuery(id+"F4.imprint","IMPRINT",FACE,{"disambiguationData":[TD([[makeQuery(id+"F4.imprint","IMPRINT",EDGE,{"derivedFrom":sQuery(id+"F4.wireOp",EDGE,"E32.0")}),1.0]])]});
            extrude(context, id + "F5", {"entities" : qUnion([Q0]), "operationType" : NewBodyOperationType.ADD, "oppositeDirection" : true, "depth" : 5 * mm});
        }
        {
            var Q0;
            {var subQ0=sQuery(id+"F0.wireOp",EDGE,"E15");var subQ1=sQuery(id+"F0.wireOp",EDGE,"E14");var subQ2=sQuery(id+"F0.wireOp",EDGE,"E13");var subQ3=sQuery(id+"F0.wireOp",EDGE,"E12");Q0=makeQuery(id+"F5.boolean.opBoolean","MERGE",FACE,{"derivedFrom":[makeQuery(id+"F1.opExtrude","CAP_FACE",FACE,{"disambiguationData":[OSD([sQuery(id+"F0.wireOp",EDGE,"E4"),sQuery(id+"F0.wireOp",EDGE,"E5.0.1.0"),sQuery(id+"F0.wireOp",EDGE,"E5.0.2.0"),sQuery(id+"F0.wireOp",EDGE,"E5.0.3.0"),sQuery(id+"F0.wireOp",EDGE,"E5.0.4.0"),sQuery(id+"F0.wireOp",EDGE,"E5.0.5.0"),sQuery(id+"F0.wireOp",EDGE,"E5.1.0.0"),sQuery(id+"F0.wireOp",EDGE,"E5.1.1.0"),sQuery(id+"F0.wireOp",EDGE,"E5.1.2.0"),sQuery(id+"F0.wireOp",EDGE,"E5.1.3.0"),sQuery(id+"F0.wireOp",EDGE,"E5.1.4.0"),sQuery(id+"F0.wireOp",EDGE,"E5.1.5.0"),sQuery(id+"F0.wireOp",EDGE,"E5.2.0.0"),sQuery(id+"F0.wireOp",EDGE,"E5.2.1.0"),sQuery(id+"F0.wireOp",EDGE,"E5.2.2.0"),sQuery(id+"F0.wireOp",EDGE,"E5.2.3.0"),sQuery(id+"F0.wireOp",EDGE,"E5.2.4.0"),sQuery(id+"F0.wireOp",EDGE,"E5.2.5.0"),sQuery(id+"F0.wireOp",EDGE,"E5.3.0.0"),sQuery(id+"F0.wireOp",EDGE,"E5.3.1.0"),sQuery(id+"F0.wireOp",EDGE,"E5.3.2.0"),sQuery(id+"F0.wireOp",EDGE,"E5.3.3.0"),sQuery(id+"F0.wireOp",EDGE,"E5.3.4.0"),sQuery(id+"F0.wireOp",EDGE,"E5.3.5.0"),sQuery(id+"F0.wireOp",EDGE,"E5.4.0.0"),sQuery(id+"F0.wireOp",EDGE,"E5.4.1.0"),sQuery(id+"F0.wireOp",EDGE,"E5.4.2.0"),sQuery(id+"F0.wireOp",EDGE,"E5.4.3.0"),sQuery(id+"F0.wireOp",EDGE,"E5.4.4.0"),sQuery(id+"F0.wireOp",EDGE,"E5.4.5.0"),sQuery(id+"F0.wireOp",EDGE,"E5.5.0.0"),sQuery(id+"F0.wireOp",EDGE,"E5.5.1.0"),sQuery(id+"F0.wireOp",EDGE,"E5.5.2.0"),sQuery(id+"F0.wireOp",EDGE,"E5.5.3.0"),sQuery(id+"F0.wireOp",EDGE,"E5.5.4.0"),sQuery(id+"F0.wireOp",EDGE,"E5.5.5.0"),sQuery(id+"F0.wireOp",EDGE,"E5.6.0.0"),sQuery(id+"F0.wireOp",EDGE,"E5.6.1.0"),sQuery(id+"F0.wireOp",EDGE,"E5.6.2.0"),sQuery(id+"F0.wireOp",EDGE,"E5.6.3.0"),sQuery(id+"F0.wireOp",EDGE,"E5.6.4.0"),sQuery(id+"F0.wireOp",EDGE,"E5.6.5.0"),sQuery(id+"F0.wireOp",EDGE,"E10.0.7.0"),sQuery(id+"F0.wireOp",EDGE,"E10.0.7.1"),sQuery(id+"F0.wireOp",EDGE,"E10.0.7.2"),sQuery(id+"F0.wireOp",EDGE,"E10.0.7.3"),sQuery(id+"F0.wireOp",EDGE,"E10.0.7.4"),sQuery(id+"F0.wireOp",EDGE,"E10.0.7.5"),sQuery(id+"F0.wireOp",EDGE,"E10.0.8.0"),sQuery(id+"F0.wireOp",EDGE,"E10.0.8.1"),sQuery(id+"F0.wireOp",EDGE,"E10.0.8.2"),sQuery(id+"F0.wireOp",EDGE,"E10.0.8.3"),sQuery(id+"F0.wireOp",EDGE,"E10.0.8.4"),sQuery(id+"F0.wireOp",EDGE,"E10.0.8.5"),sQuery(id+"F0.wireOp",EDGE,"E11.0.9.0"),sQuery(id+"F0.wireOp",EDGE,"E11.0.9.1"),sQuery(id+"F0.wireOp",EDGE,"E11.0.9.2"),sQuery(id+"F0.wireOp",EDGE,"E11.0.9.3"),sQuery(id+"F0.wireOp",EDGE,"E11.0.9.4"),sQuery(id+"F0.wireOp",EDGE,"E11.0.9.5"),subQ3,subQ2,subQ1,subQ0,sQuery(id+"F0.wireOp",EDGE,"E19.0.0.6"),sQuery(id+"F0.wireOp",EDGE,"E19.0.0.7"),sQuery(id+"F0.wireOp",EDGE,"E19.0.1.6"),sQuery(id+"F0.wireOp",EDGE,"E19.0.1.7"),sQuery(id+"F0.wireOp",EDGE,"E19.0.2.6"),sQuery(id+"F0.wireOp",EDGE,"E19.0.2.7"),sQuery(id+"F0.wireOp",EDGE,"E19.0.3.6"),sQuery(id+"F0.wireOp",EDGE,"E19.0.3.7"),sQuery(id+"F0.wireOp",EDGE,"E19.0.4.6"),sQuery(id+"F0.wireOp",EDGE,"E19.0.4.7"),sQuery(id+"F0.wireOp",EDGE,"E19.0.5.6"),sQuery(id+"F0.wireOp",EDGE,"E19.0.5.7"),sQuery(id+"F0.wireOp",EDGE,"E19.0.6.6"),sQuery(id+"F0.wireOp",EDGE,"E19.0.6.7"),sQuery(id+"F0.wireOp",EDGE,"E19.0.7.6"),sQuery(id+"F0.wireOp",EDGE,"E19.0.7.7"),sQuery(id+"F0.wireOp",EDGE,"E19.0.8.6"),sQuery(id+"F0.wireOp",EDGE,"E19.0.8.7"),sQuery(id+"F0.wireOp",EDGE,"E19.0.9.6"),sQuery(id+"F0.wireOp",EDGE,"E19.0.9.7"),sQuery(id+"F0.wireOp",EDGE,"E20"),sQuery(id+"F0.wireOp",EDGE,"E21.0.1.0"),sQuery(id+"F0.wireOp",EDGE,"E21.0.2.0"),sQuery(id+"F0.wireOp",EDGE,"E21.0.3.0"),sQuery(id+"F0.wireOp",EDGE,"E21.0.4.0"),sQuery(id+"F0.wireOp",EDGE,"E21.0.5.0"),sQuery(id+"F0.wireOp",EDGE,"E21.0.6.0"),sQuery(id+"F0.wireOp",EDGE,"E21.1.0.0"),sQuery(id+"F0.wireOp",EDGE,"E21.1.1.0"),sQuery(id+"F0.wireOp",EDGE,"E21.1.2.0"),sQuery(id+"F0.wireOp",EDGE,"E21.1.3.0"),sQuery(id+"F0.wireOp",EDGE,"E21.1.4.0"),sQuery(id+"F0.wireOp",EDGE,"E21.1.5.0"),sQuery(id+"F0.wireOp",EDGE,"E21.1.6.0"),sQuery(id+"F0.wireOp",EDGE,"E21.2.0.0"),sQuery(id+"F0.wireOp",EDGE,"E21.2.1.0"),sQuery(id+"F0.wireOp",EDGE,"E21.2.2.0"),sQuery(id+"F0.wireOp",EDGE,"E21.2.3.0"),sQuery(id+"F0.wireOp",EDGE,"E21.2.4.0"),sQuery(id+"F0.wireOp",EDGE,"E21.2.5.0"),sQuery(id+"F0.wireOp",EDGE,"E21.2.6.0"),sQuery(id+"F0.wireOp",EDGE,"E21.3.0.0"),sQuery(id+"F0.wireOp",EDGE,"E21.3.1.0"),sQuery(id+"F0.wireOp",EDGE,"E21.3.2.0"),sQuery(id+"F0.wireOp",EDGE,"E21.3.3.0"),sQuery(id+"F0.wireOp",EDGE,"E21.3.4.0"),sQuery(id+"F0.wireOp",EDGE,"E21.3.5.0"),sQuery(id+"F0.wireOp",EDGE,"E21.3.6.0"),sQuery(id+"F0.wireOp",EDGE,"E21.4.0.0"),sQuery(id+"F0.wireOp",EDGE,"E21.4.1.0"),sQuery(id+"F0.wireOp",EDGE,"E21.4.2.0"),sQuery(id+"F0.wireOp",EDGE,"E21.4.3.0"),sQuery(id+"F0.wireOp",EDGE,"E21.4.4.0"),sQuery(id+"F0.wireOp",EDGE,"E21.4.5.0"),sQuery(id+"F0.wireOp",EDGE,"E21.4.6.0"),sQuery(id+"F0.wireOp",EDGE,"E21.5.0.0"),sQuery(id+"F0.wireOp",EDGE,"E21.5.1.0"),sQuery(id+"F0.wireOp",EDGE,"E21.5.2.0"),sQuery(id+"F0.wireOp",EDGE,"E21.5.3.0"),sQuery(id+"F0.wireOp",EDGE,"E21.5.4.0"),sQuery(id+"F0.wireOp",EDGE,"E21.5.5.0"),sQuery(id+"F0.wireOp",EDGE,"E21.5.6.0"),sQuery(id+"F0.wireOp",EDGE,"E21.6.0.0"),sQuery(id+"F0.wireOp",EDGE,"E21.6.1.0"),sQuery(id+"F0.wireOp",EDGE,"E21.6.2.0"),sQuery(id+"F0.wireOp",EDGE,"E21.6.3.0"),sQuery(id+"F0.wireOp",EDGE,"E21.6.4.0"),sQuery(id+"F0.wireOp",EDGE,"E21.6.5.0"),sQuery(id+"F0.wireOp",EDGE,"E21.6.6.0"),sQuery(id+"F0.wireOp",EDGE,"E21.7.0.0"),sQuery(id+"F0.wireOp",EDGE,"E21.7.1.0"),sQuery(id+"F0.wireOp",EDGE,"E21.7.2.0"),sQuery(id+"F0.wireOp",EDGE,"E21.7.3.0"),sQuery(id+"F0.wireOp",EDGE,"E21.7.4.0"),sQuery(id+"F0.wireOp",EDGE,"E21.7.5.0"),sQuery(id+"F0.wireOp",EDGE,"E21.7.6.0"),sQuery(id+"F0.wireOp",EDGE,"E21.8.0.0"),sQuery(id+"F0.wireOp",EDGE,"E21.8.1.0"),sQuery(id+"F0.wireOp",EDGE,"E21.8.2.0"),sQuery(id+"F0.wireOp",EDGE,"E21.8.3.0"),sQuery(id+"F0.wireOp",EDGE,"E21.8.4.0"),sQuery(id+"F0.wireOp",EDGE,"E21.8.5.0"),sQuery(id+"F0.wireOp",EDGE,"E21.8.6.0"),sQuery(id+"F0.wireOp",EDGE,"E21.9.0.0"),sQuery(id+"F0.wireOp",EDGE,"E21.9.1.0"),sQuery(id+"F0.wireOp",EDGE,"E21.9.2.0"),sQuery(id+"F0.wireOp",EDGE,"E21.9.3.0"),sQuery(id+"F0.wireOp",EDGE,"E21.9.4.0"),sQuery(id+"F0.wireOp",EDGE,"E21.9.5.0"),sQuery(id+"F0.wireOp",EDGE,"E21.9.6.0"),sQuery(id+"F0.wireOp",EDGE,"E25.0.0.7"),sQuery(id+"F0.wireOp",EDGE,"E25.0.1.7"),sQuery(id+"F0.wireOp",EDGE,"E25.0.2.7"),sQuery(id+"F0.wireOp",EDGE,"E25.0.3.7"),sQuery(id+"F0.wireOp",EDGE,"E25.0.4.7"),sQuery(id+"F0.wireOp",EDGE,"E25.0.5.7"),sQuery(id+"F0.wireOp",EDGE,"E25.0.6.7"),sQuery(id+"F0.wireOp",EDGE,"E25.0.7.7"),sQuery(id+"F0.wireOp",EDGE,"E25.0.8.7"),sQuery(id+"F0.wireOp",EDGE,"E25.0.9.7")])],"isStart":true}),makeQuery(id+"F5.opExtrude","CAP_FACE",FACE,{"disambiguationData":[OSD([subQ3,subQ2,subQ1,subQ0,sQuery(id+"F4.wireOp",EDGE,"E32.0"),sQuery(id+"F4.wireOp",EDGE,"E32.1"),sQuery(id+"F4.wireOp",EDGE,"E32.2"),sQuery(id+"F4.wireOp",EDGE,"E32.3")])],"isStart":true})]});}
            extrude(context, id + "F6", {"entities" : qUnion([Q0]), "depth" : 1 * mm});
        }
    });
